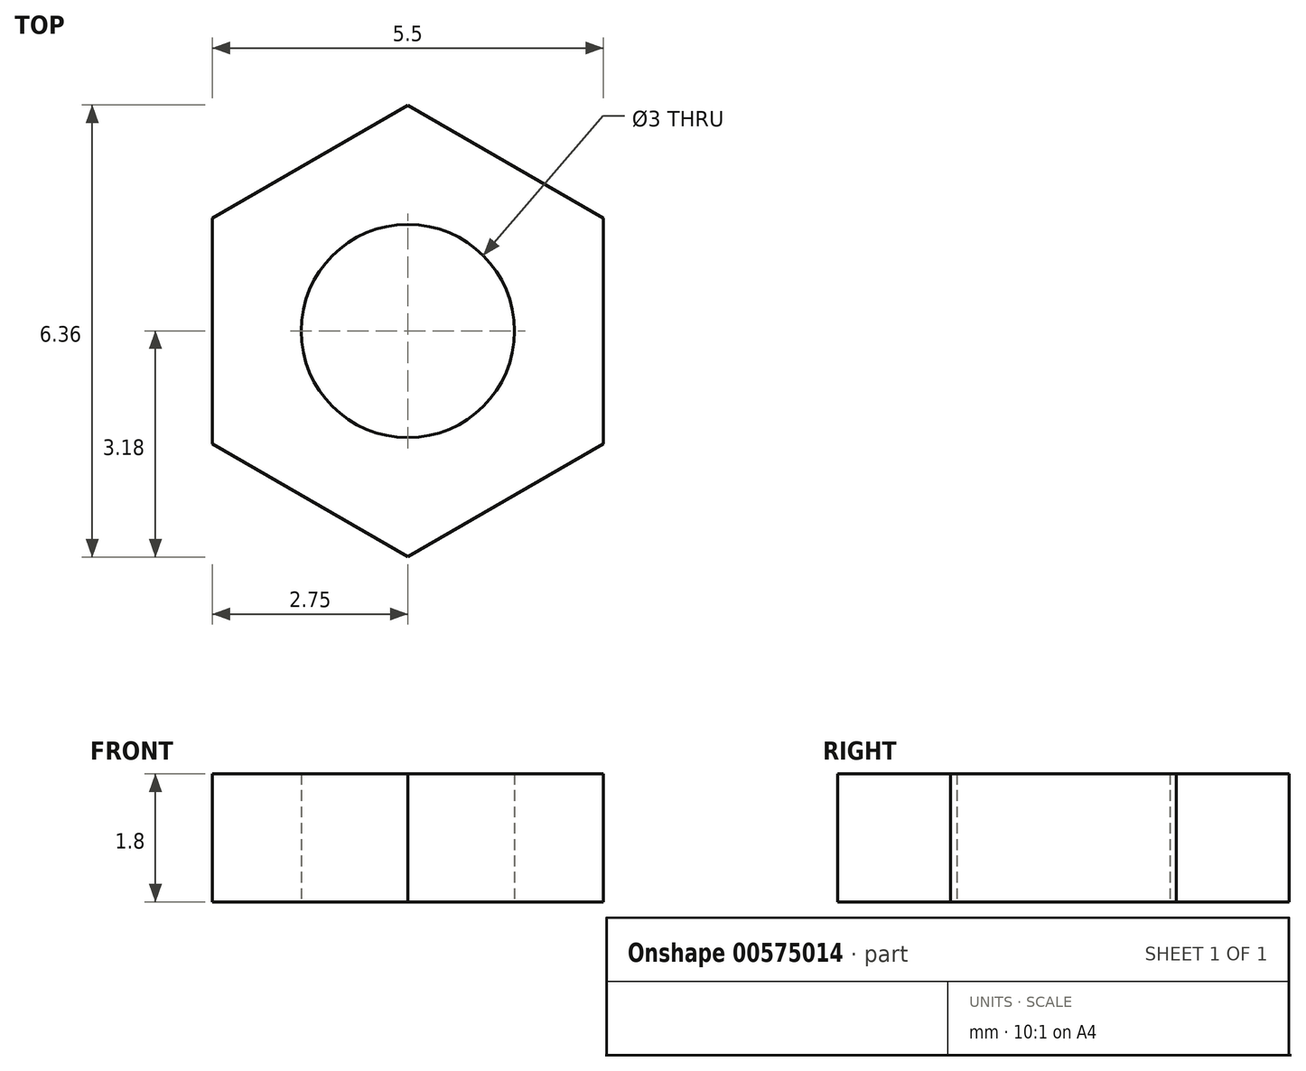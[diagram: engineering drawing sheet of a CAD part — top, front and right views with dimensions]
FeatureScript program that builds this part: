
annotation { "Feature Type Name" : "Feature", "Feature Type Description" : "" }
export const myFeature = defineFeature(function(context is Context, id is Id, definition is map)
    precondition{}
    {
        {
            var Q0;
            Q0=qCreatedBy(makeId("Top.planeOp"),FACE);
            var sketch = newSketch(context, id + "F0", { "sketchPlane" : qUnion([Q0])});
            skCircle(sketch, "E0.cCircle", {"center": v(0, 0) * mm, "radius": 2.75 * mm, "construction": true});
            skLineSegment(sketch, "E0.0", {"start": v(-2.75, 1.59) * mm, "end": v(0, 3.18) * mm});
            skLineSegment(sketch, "E0.1", {"start": v(0, 3.18) * mm, "end": v(2.75, 1.59) * mm});
            skLineSegment(sketch, "E0.2", {"start": v(2.75, 1.59) * mm, "end": v(2.75, -1.59) * mm});
            skLineSegment(sketch, "E0.3", {"start": v(2.75, -1.59) * mm, "end": v(0, -3.18) * mm});
            skLineSegment(sketch, "E0.4", {"start": v(0, -3.18) * mm, "end": v(-2.75, -1.59) * mm});
            skLineSegment(sketch, "E0.5", {"start": v(-2.75, -1.59) * mm, "end": v(-2.75, 1.59) * mm});
            skPoint(sketch, "E0.0.midPoint", {"position": v(-1.38, 2.38) * mm});
            skCircle(sketch, "E1", {"center": v(0, 0) * mm, "radius": 1.5 * mm});
            skSolve(sketch);
        }
        {
            var Q0;
            Q0 = qSketchRegion(id + "F0", true);
            extrude(context, id + "F1", {"entities" : qUnion([Q0]), "depth" : 1.8 * mm, "offsetDistance" : 25 * mm});
        }
    });
